FCSTD DOCUMENT  (FreeCAD 1.0R39319 (Git))
Label: 3BHK_House_Blueprint1
License: All rights reserved
LicenseURL: https://en.wikipedia.org/wiki/All_rights_reserved
objects: App::FeaturePython×51, Part::Part2DObjectPython×46
note: 46 computed .brp shape members not serialized (recipe doc carries the construction recipe); baked Part::Feature solids carry a one-line shape summary decoded from their .brp

FEATURE [Part::Part2DObjectPython] Wire  # Draft 2D object (typed FeaturePython)
  Area = 90000000
  ChamferSize = 0
  Closed = true
  End = (0,0,0)
  FilletRadius = 0
  Length = 42000
  MakeFace = true
  Points = (5) [(0,0,0),(15000,0,0),(15000,6000,0),(0,6000,0),(0,0,0)]
  Start = (0,0,0)
  Subdivisions = 0
FEATURE [Part::Part2DObjectPython] Line  # Draft 2D object (typed FeaturePython)
  Area = 0
  ChamferSize = 0
  Closed = false
  End = (3000,0,0)
  FilletRadius = 0
  Length = 1000
  MakeFace = true
  Points = (2) [(2000,0,0),(3000,0,0)]
  Start = (2000,0,0)
  Subdivisions = 0
FEATURE [Part::Part2DObjectPython] Rectangle  # Draft 2D object (typed FeaturePython)
  Area = 960000
  ChamferSize = 0
  Columns = 1
  FilletRadius = 0
  Height = 1200
  Length = 800
  MakeFace = true
  Placement = pos=(4000,1000,0) rot=(0,0,1;0rad)
  Rows = 1
FEATURE [Part::Part2DObjectPython] Rectangle001  # Draft 2D object (typed FeaturePython)
  Area = 960000
  ChamferSize = 0
  Columns = 1
  FilletRadius = 0
  Height = 1200
  Length = 800
  MakeFace = true
  Placement = pos=(9000,1000,0) rot=(0,0,1;0rad)
  Rows = 1
FEATURE [App::FeaturePython] Dimension  # Draft dimension (typed FeaturePython)
  Diameter = false
  Dimline = (7500,-500,0)
  Direction = (0,0,0)
  Distance = 15000
  End = (15000,-500,0)
  Normal = (0,0,1)
  Start = (0,-500,0)
FEATURE [App::FeaturePython] Dimension001  # Draft dimension (typed FeaturePython)
  Diameter = false
  Dimline = (0,3000,0)
  Direction = (0,0,0)
  Distance = 6000
  End = (0,6000,0)
  Normal = (0,0,1)
  Start = (0,0,0)
FEATURE [App::FeaturePython] Text  # WARN: FeaturePython — macro-defined, semantics opaque (R4)
  Placement = pos=(2500,-500,0) rot=(0,0,1;0rad)
  Text = Main Door
FEATURE [App::FeaturePython] Text001  # WARN: FeaturePython — macro-defined, semantics opaque (R4)
  Placement = pos=(4500,1500,0) rot=(0,0,1;0rad)
  Text = Window 1
FEATURE [App::FeaturePython] Text002  # WARN: FeaturePython — macro-defined, semantics opaque (R4)
  Placement = pos=(9500,1500,0) rot=(0,0,1;0rad)
  Text = Window 2
FEATURE [Part::Part2DObjectPython] Rectangle002  # Draft 2D object (typed FeaturePython)
  Area = 1.2e+07
  ChamferSize = 0
  Columns = 1
  FilletRadius = 0
  Height = 3000
  Length = 4000
  MakeFace = true
  Placement = pos=(2000,10000,0) rot=(0,0,1;0rad)
  Rows = 1
FEATURE [Part::Part2DObjectPython] Rectangle003  # Draft 2D object (typed FeaturePython)
  Area = 4e+06
  ChamferSize = 0
  Columns = 1
  FilletRadius = 0
  Height = 2000
  Length = 2000
  MakeFace = true
  Placement = pos=(8000,10000,0) rot=(0,0,1;0rad)
  Rows = 1
FEATURE [Part::Part2DObjectPython] Rectangle004  # Draft 2D object (typed FeaturePython)
  Area = 9000000
  ChamferSize = 0
  Columns = 1
  FilletRadius = 0
  Height = 3000
  Length = 3000
  MakeFace = true
  Placement = pos=(2000,13000,0) rot=(0,0,1;0rad)
  Rows = 1
FEATURE [Part::Part2DObjectPython] Rectangle005  # Draft 2D object (typed FeaturePython)
  Area = 9000000
  ChamferSize = 0
  Columns = 1
  FilletRadius = 0
  Height = 3000
  Length = 3000
  MakeFace = true
  Placement = pos=(6000,13000,0) rot=(0,0,1;0rad)
  Rows = 1
FEATURE [Part::Part2DObjectPython] Rectangle006  # Draft 2D object (typed FeaturePython)
  Area = 9000000
  ChamferSize = 0
  Columns = 1
  FilletRadius = 0
  Height = 3000
  Length = 3000
  MakeFace = true
  Placement = pos=(10000,13000,0) rot=(0,0,1;0rad)
  Rows = 1
FEATURE [Part::Part2DObjectPython] Rectangle007  # Draft 2D object (typed FeaturePython)
  Area = 2.4e+07
  ChamferSize = 0
  Columns = 1
  FilletRadius = 0
  Height = 6000
  Length = 4000
  MakeFace = true
  Placement = pos=(0,10000,0) rot=(0,0,1;0rad)
  Rows = 1
FEATURE [Part::Part2DObjectPython] Rectangle008  # Draft 2D object (typed FeaturePython)
  Area = 1.6e+07
  ChamferSize = 0
  Columns = 1
  FilletRadius = 0
  Height = 4000
  Length = 4000
  MakeFace = true
  Placement = pos=(12000,10000,0) rot=(0,0,1;0rad)
  Rows = 1
FEATURE [App::FeaturePython] Dimension002  # Draft dimension (typed FeaturePython)
  Diameter = false
  Dimline = (7500,10000,0)
  Direction = (0,0,0)
  Distance = 15000
  End = (15000,10000,0)
  Normal = (0,0,1)
  Start = (0,10000,0)
FEATURE [App::FeaturePython] Dimension003  # Draft dimension (typed FeaturePython)
  Diameter = false
  Dimline = (0,13000,0)
  Direction = (0,0,0)
  Distance = 6000
  End = (0,16000,0)
  Normal = (0,0,1)
  Start = (0,10000,0)
FEATURE [App::FeaturePython] Text003  # WARN: FeaturePython — macro-defined, semantics opaque (R4)
  Placement = pos=(3000,10500,0) rot=(0,0,1;0rad)
  Text = Living Room
FEATURE [App::FeaturePython] Text004  # WARN: FeaturePython — macro-defined, semantics opaque (R4)
  Placement = pos=(9000,10500,0) rot=(0,0,1;0rad)
  Text = Kitchen
FEATURE [App::FeaturePython] Text005  # WARN: FeaturePython — macro-defined, semantics opaque (R4)
  Placement = pos=(3000,13500,0) rot=(0,0,1;0rad)
  Text = Bedroom 1
FEATURE [App::FeaturePython] Text006  # WARN: FeaturePython — macro-defined, semantics opaque (R4)
  Placement = pos=(7000,13500,0) rot=(0,0,1;0rad)
  Text = Bedroom 2
FEATURE [App::FeaturePython] Text007  # WARN: FeaturePython — macro-defined, semantics opaque (R4)
  Placement = pos=(11000,13500,0) rot=(0,0,1;0rad)
  Text = Bedroom 3
FEATURE [App::FeaturePython] Text008  # WARN: FeaturePython — macro-defined, semantics opaque (R4)
  Placement = pos=(2000,10500,0) rot=(0,0,1;0rad)
  Text = Parking
FEATURE [App::FeaturePython] Text009  # WARN: FeaturePython — macro-defined, semantics opaque (R4)
  Placement = pos=(13000,10500,0) rot=(0,0,1;0rad)
  Text = Garden
FEATURE [Part::Part2DObjectPython] Wire001  # Draft 2D object (typed FeaturePython)
  Area = 90000000
  ChamferSize = 0
  Closed = true
  End = (0,20000,0)
  FilletRadius = 0
  Length = 42000
  MakeFace = true
  Points = (5) [(0,20000,0),(15000,20000,0),(15000,26000,0),(0,26000,0),(0,20000,0)]
  Start = (0,20000,0)
  Subdivisions = 0
FEATURE [Part::Part2DObjectPython] Line001  # Draft 2D object (typed FeaturePython)
  Area = 0
  ChamferSize = 0
  Closed = false
  End = (3000,20000,0)
  FilletRadius = 0
  Length = 1000
  MakeFace = true
  Points = (2) [(2000,20000,0),(3000,20000,0)]
  Start = (2000,20000,0)
  Subdivisions = 0
FEATURE [Part::Part2DObjectPython] Rectangle009  # Draft 2D object (typed FeaturePython)
  Area = 960000
  ChamferSize = 0
  Columns = 1
  FilletRadius = 0
  Height = 1200
  Length = 800
  MakeFace = true
  Placement = pos=(4000,21000,0) rot=(0,0,1;0rad)
  Rows = 1
FEATURE [App::FeaturePython] Dimension004  # Draft dimension (typed FeaturePython)
  Diameter = false
  Dimline = (7500,20000,0)
  Direction = (0,0,0)
  Distance = 15000
  End = (15000,20000,0)
  Normal = (0,0,1)
  Start = (0,20000,0)
FEATURE [App::FeaturePython] Dimension005  # Draft dimension (typed FeaturePython)
  Diameter = false
  Dimline = (0,23000,0)
  Direction = (0,0,0)
  Distance = 6000
  End = (0,26000,0)
  Normal = (0,0,1)
  Start = (0,20000,0)
FEATURE [App::FeaturePython] Text010  # WARN: FeaturePython — macro-defined, semantics opaque (R4)
  Placement = pos=(2500,20000,0) rot=(0,0,1;0rad)
  Text = Door 2
FEATURE [App::FeaturePython] Text011  # WARN: FeaturePython — macro-defined, semantics opaque (R4)
  Placement = pos=(4500,21000,0) rot=(0,0,1;0rad)
  Text = Window 3
FEATURE [Part::Part2DObjectPython] Line002  # Draft 2D object (typed FeaturePython)
  Area = 0
  ChamferSize = 0
  Closed = false
  End = (0,6000,0)
  FilletRadius = 0
  Length = 6000
  MakeFace = true
  Points = (2) [(0,0,0),(0,6000,0)]
  Start = (0,0,0)
  Subdivisions = 0
FEATURE [App::FeaturePython] Text012  # WARN: FeaturePython — macro-defined, semantics opaque (R4)
  Placement = pos=(0,-500,0) rot=(0,0,1;0rad)
  Text = A
FEATURE [Part::Part2DObjectPython] Line003  # Draft 2D object (typed FeaturePython)
  Area = 0
  ChamferSize = 0
  Closed = false
  End = (1000,6000,0)
  FilletRadius = 0
  Length = 6000
  MakeFace = true
  Points = (2) [(1000,0,0),(1000,6000,0)]
  Start = (1000,0,0)
  Subdivisions = 0
FEATURE [App::FeaturePython] Text013  # WARN: FeaturePython — macro-defined, semantics opaque (R4)
  Placement = pos=(1000,-500,0) rot=(0,0,1;0rad)
  Text = B
FEATURE [Part::Part2DObjectPython] Line004  # Draft 2D object (typed FeaturePython)
  Area = 0
  ChamferSize = 0
  Closed = false
  End = (2000,6000,0)
  FilletRadius = 0
  Length = 6000
  MakeFace = true
  Points = (2) [(2000,0,0),(2000,6000,0)]
  Start = (2000,0,0)
  Subdivisions = 0
FEATURE [App::FeaturePython] Text014  # WARN: FeaturePython — macro-defined, semantics opaque (R4)
  Placement = pos=(2000,-500,0) rot=(0,0,1;0rad)
  Text = C
FEATURE [Part::Part2DObjectPython] Line005  # Draft 2D object (typed FeaturePython)
  Area = 0
  ChamferSize = 0
  Closed = false
  End = (3000,6000,0)
  FilletRadius = 0
  Length = 6000
  MakeFace = true
  Points = (2) [(3000,0,0),(3000,6000,0)]
  Start = (3000,0,0)
  Subdivisions = 0
FEATURE [App::FeaturePython] Text015  # WARN: FeaturePython — macro-defined, semantics opaque (R4)
  Placement = pos=(3000,-500,0) rot=(0,0,1;0rad)
  Text = D
FEATURE [Part::Part2DObjectPython] Line006  # Draft 2D object (typed FeaturePython)
  Area = 0
  ChamferSize = 0
  Closed = false
  End = (4000,6000,0)
  FilletRadius = 0
  Length = 6000
  MakeFace = true
  Points = (2) [(4000,0,0),(4000,6000,0)]
  Start = (4000,0,0)
  Subdivisions = 0
FEATURE [App::FeaturePython] Text016  # WARN: FeaturePython — macro-defined, semantics opaque (R4)
  Placement = pos=(4000,-500,0) rot=(0,0,1;0rad)
  Text = E
FEATURE [Part::Part2DObjectPython] Line007  # Draft 2D object (typed FeaturePython)
  Area = 0
  ChamferSize = 0
  Closed = false
  End = (5000,6000,0)
  FilletRadius = 0
  Length = 6000
  MakeFace = true
  Points = (2) [(5000,0,0),(5000,6000,0)]
  Start = (5000,0,0)
  Subdivisions = 0
FEATURE [App::FeaturePython] Text017  # WARN: FeaturePython — macro-defined, semantics opaque (R4)
  Placement = pos=(5000,-500,0) rot=(0,0,1;0rad)
  Text = F
FEATURE [Part::Part2DObjectPython] Line008  # Draft 2D object (typed FeaturePython)
  Area = 0
  ChamferSize = 0
  Closed = false
  End = (6000,6000,0)
  FilletRadius = 0
  Length = 6000
  MakeFace = true
  Points = (2) [(6000,0,0),(6000,6000,0)]
  Start = (6000,0,0)
  Subdivisions = 0
FEATURE [App::FeaturePython] Text018  # WARN: FeaturePython — macro-defined, semantics opaque (R4)
  Placement = pos=(6000,-500,0) rot=(0,0,1;0rad)
  Text = G
FEATURE [Part::Part2DObjectPython] Line009  # Draft 2D object (typed FeaturePython)
  Area = 0
  ChamferSize = 0
  Closed = false
  End = (7000,6000,0)
  FilletRadius = 0
  Length = 6000
  MakeFace = true
  Points = (2) [(7000,0,0),(7000,6000,0)]
  Start = (7000,0,0)
  Subdivisions = 0
FEATURE [App::FeaturePython] Text019  # WARN: FeaturePython — macro-defined, semantics opaque (R4)
  Placement = pos=(7000,-500,0) rot=(0,0,1;0rad)
  Text = H
FEATURE [Part::Part2DObjectPython] Line010  # Draft 2D object (typed FeaturePython)
  Area = 0
  ChamferSize = 0
  Closed = false
  End = (8000,6000,0)
  FilletRadius = 0
  Length = 6000
  MakeFace = true
  Points = (2) [(8000,0,0),(8000,6000,0)]
  Start = (8000,0,0)
  Subdivisions = 0
FEATURE [App::FeaturePython] Text020  # WARN: FeaturePython — macro-defined, semantics opaque (R4)
  Placement = pos=(8000,-500,0) rot=(0,0,1;0rad)
  Text = I
FEATURE [Part::Part2DObjectPython] Line011  # Draft 2D object (typed FeaturePython)
  Area = 0
  ChamferSize = 0
  Closed = false
  End = (9000,6000,0)
  FilletRadius = 0
  Length = 6000
  MakeFace = true
  Points = (2) [(9000,0,0),(9000,6000,0)]
  Start = (9000,0,0)
  Subdivisions = 0
FEATURE [App::FeaturePython] Text021  # WARN: FeaturePython — macro-defined, semantics opaque (R4)
  Placement = pos=(9000,-500,0) rot=(0,0,1;0rad)
  Text = J
FEATURE [Part::Part2DObjectPython] Line012  # Draft 2D object (typed FeaturePython)
  Area = 0
  ChamferSize = 0
  Closed = false
  End = (10000,6000,0)
  FilletRadius = 0
  Length = 6000
  MakeFace = true
  Points = (2) [(10000,0,0),(10000,6000,0)]
  Start = (10000,0,0)
  Subdivisions = 0
FEATURE [App::FeaturePython] Text022  # WARN: FeaturePython — macro-defined, semantics opaque (R4)
  Placement = pos=(10000,-500,0) rot=(0,0,1;0rad)
  Text = K
FEATURE [Part::Part2DObjectPython] Line013  # Draft 2D object (typed FeaturePython)
  Area = 0
  ChamferSize = 0
  Closed = false
  End = (11000,6000,0)
  FilletRadius = 0
  Length = 6000
  MakeFace = true
  Points = (2) [(11000,0,0),(11000,6000,0)]
  Start = (11000,0,0)
  Subdivisions = 0
FEATURE [App::FeaturePython] Text023  # WARN: FeaturePython — macro-defined, semantics opaque (R4)
  Placement = pos=(11000,-500,0) rot=(0,0,1;0rad)
  Text = L
FEATURE [Part::Part2DObjectPython] Line014  # Draft 2D object (typed FeaturePython)
  Area = 0
  ChamferSize = 0
  Closed = false
  End = (12000,6000,0)
  FilletRadius = 0
  Length = 6000
  MakeFace = true
  Points = (2) [(12000,0,0),(12000,6000,0)]
  Start = (12000,0,0)
  Subdivisions = 0
FEATURE [App::FeaturePython] Text024  # WARN: FeaturePython — macro-defined, semantics opaque (R4)
  Placement = pos=(12000,-500,0) rot=(0,0,1;0rad)
  Text = M
FEATURE [Part::Part2DObjectPython] Line015  # Draft 2D object (typed FeaturePython)
  Area = 0
  ChamferSize = 0
  Closed = false
  End = (13000,6000,0)
  FilletRadius = 0
  Length = 6000
  MakeFace = true
  Points = (2) [(13000,0,0),(13000,6000,0)]
  Start = (13000,0,0)
  Subdivisions = 0
FEATURE [App::FeaturePython] Text025  # WARN: FeaturePython — macro-defined, semantics opaque (R4)
  Placement = pos=(13000,-500,0) rot=(0,0,1;0rad)
  Text = N
FEATURE [Part::Part2DObjectPython] Line016  # Draft 2D object (typed FeaturePython)
  Area = 0
  ChamferSize = 0
  Closed = false
  End = (14000,6000,0)
  FilletRadius = 0
  Length = 6000
  MakeFace = true
  Points = (2) [(14000,0,0),(14000,6000,0)]
  Start = (14000,0,0)
  Subdivisions = 0
FEATURE [App::FeaturePython] Text026  # WARN: FeaturePython — macro-defined, semantics opaque (R4)
  Placement = pos=(14000,-500,0) rot=(0,0,1;0rad)
  Text = O
FEATURE [Part::Part2DObjectPython] Line017  # Draft 2D object (typed FeaturePython)
  Area = 0
  ChamferSize = 0
  Closed = false
  End = (15000,6000,0)
  FilletRadius = 0
  Length = 6000
  MakeFace = true
  Points = (2) [(15000,0,0),(15000,6000,0)]
  Start = (15000,0,0)
  Subdivisions = 0
FEATURE [App::FeaturePython] Text027  # WARN: FeaturePython — macro-defined, semantics opaque (R4)
  Placement = pos=(15000,-500,0) rot=(0,0,1;0rad)
  Text = P
FEATURE [Part::Part2DObjectPython] Line018  # Draft 2D object (typed FeaturePython)
  Area = 0
  ChamferSize = 0
  Closed = false
  End = (15000,0,0)
  FilletRadius = 0
  Length = 15000
  MakeFace = true
  Points = (2) [(0,0,0),(15000,0,0)]
  Start = (0,0,0)
  Subdivisions = 0
FEATURE [App::FeaturePython] Text028  # WARN: FeaturePython — macro-defined, semantics opaque (R4)
  Placement = pos=(-500,0,0) rot=(0,0,1;0rad)
  Text = 1
FEATURE [Part::Part2DObjectPython] Line019  # Draft 2D object (typed FeaturePython)
  Area = 0
  ChamferSize = 0
  Closed = false
  End = (15000,1000,0)
  FilletRadius = 0
  Length = 15000
  MakeFace = true
  Points = (2) [(0,1000,0),(15000,1000,0)]
  Start = (0,1000,0)
  Subdivisions = 0
FEATURE [App::FeaturePython] Text029  # WARN: FeaturePython — macro-defined, semantics opaque (R4)
  Placement = pos=(-500,1000,0) rot=(0,0,1;0rad)
  Text = 2
FEATURE [Part::Part2DObjectPython] Line020  # Draft 2D object (typed FeaturePython)
  Area = 0
  ChamferSize = 0
  Closed = false
  End = (15000,2000,0)
  FilletRadius = 0
  Length = 15000
  MakeFace = true
  Points = (2) [(0,2000,0),(15000,2000,0)]
  Start = (0,2000,0)
  Subdivisions = 0
FEATURE [App::FeaturePython] Text030  # WARN: FeaturePython — macro-defined, semantics opaque (R4)
  Placement = pos=(-500,2000,0) rot=(0,0,1;0rad)
  Text = 3
FEATURE [Part::Part2DObjectPython] Line021  # Draft 2D object (typed FeaturePython)
  Area = 0
  ChamferSize = 0
  Closed = false
  End = (15000,3000,0)
  FilletRadius = 0
  Length = 15000
  MakeFace = true
  Points = (2) [(0,3000,0),(15000,3000,0)]
  Start = (0,3000,0)
  Subdivisions = 0
FEATURE [App::FeaturePython] Text031  # WARN: FeaturePython — macro-defined, semantics opaque (R4)
  Placement = pos=(-500,3000,0) rot=(0,0,1;0rad)
  Text = 4
FEATURE [Part::Part2DObjectPython] Line022  # Draft 2D object (typed FeaturePython)
  Area = 0
  ChamferSize = 0
  Closed = false
  End = (15000,4000,0)
  FilletRadius = 0
  Length = 15000
  MakeFace = true
  Points = (2) [(0,4000,0),(15000,4000,0)]
  Start = (0,4000,0)
  Subdivisions = 0
FEATURE [App::FeaturePython] Text032  # WARN: FeaturePython — macro-defined, semantics opaque (R4)
  Placement = pos=(-500,4000,0) rot=(0,0,1;0rad)
  Text = 5
FEATURE [Part::Part2DObjectPython] Line023  # Draft 2D object (typed FeaturePython)
  Area = 0
  ChamferSize = 0
  Closed = false
  End = (15000,5000,0)
  FilletRadius = 0
  Length = 15000
  MakeFace = true
  Points = (2) [(0,5000,0),(15000,5000,0)]
  Start = (0,5000,0)
  Subdivisions = 0
FEATURE [App::FeaturePython] Text033  # WARN: FeaturePython — macro-defined, semantics opaque (R4)
  Placement = pos=(-500,5000,0) rot=(0,0,1;0rad)
  Text = 6
FEATURE [Part::Part2DObjectPython] Line024  # Draft 2D object (typed FeaturePython)
  Area = 0
  ChamferSize = 0
  Closed = false
  End = (15000,6000,0)
  FilletRadius = 0
  Length = 15000
  MakeFace = true
  Points = (2) [(0,6000,0),(15000,6000,0)]
  Start = (0,6000,0)
  Subdivisions = 0
FEATURE [App::FeaturePython] Text034  # WARN: FeaturePython — macro-defined, semantics opaque (R4)
  Placement = pos=(-500,6000,0) rot=(0,0,1;0rad)
  Text = 7
FEATURE [Part::Part2DObjectPython] Line025  # Draft 2D object (typed FeaturePython)
  Area = 0
  ChamferSize = 0
  Closed = false
  End = (15000,7000,0)
  FilletRadius = 0
  Length = 15000
  MakeFace = true
  Points = (2) [(0,7000,0),(15000,7000,0)]
  Start = (0,7000,0)
  Subdivisions = 0
FEATURE [App::FeaturePython] Text035  # WARN: FeaturePython — macro-defined, semantics opaque (R4)
  Placement = pos=(-500,7000,0) rot=(0,0,1;0rad)
  Text = 8
FEATURE [Part::Part2DObjectPython] Line026  # Draft 2D object (typed FeaturePython)
  Area = 0
  ChamferSize = 0
  Closed = false
  End = (15000,8000,0)
  FilletRadius = 0
  Length = 15000
  MakeFace = true
  Points = (2) [(0,8000,0),(15000,8000,0)]
  Start = (0,8000,0)
  Subdivisions = 0
FEATURE [App::FeaturePython] Text036  # WARN: FeaturePython — macro-defined, semantics opaque (R4)
  Placement = pos=(-500,8000,0) rot=(0,0,1;0rad)
  Text = 9
FEATURE [Part::Part2DObjectPython] Line027  # Draft 2D object (typed FeaturePython)
  Area = 0
  ChamferSize = 0
  Closed = false
  End = (15000,9000,0)
  FilletRadius = 0
  Length = 15000
  MakeFace = true
  Points = (2) [(0,9000,0),(15000,9000,0)]
  Start = (0,9000,0)
  Subdivisions = 0
FEATURE [App::FeaturePython] Text037  # WARN: FeaturePython — macro-defined, semantics opaque (R4)
  Placement = pos=(-500,9000,0) rot=(0,0,1;0rad)
  Text = 10
FEATURE [Part::Part2DObjectPython] Line028  # Draft 2D object (typed FeaturePython)
  Area = 0
  ChamferSize = 0
  Closed = false
  End = (15000,10000,0)
  FilletRadius = 0
  Length = 15000
  MakeFace = true
  Points = (2) [(0,10000,0),(15000,10000,0)]
  Start = (0,10000,0)
  Subdivisions = 0
FEATURE [App::FeaturePython] Text038  # WARN: FeaturePython — macro-defined, semantics opaque (R4)
  Placement = pos=(-500,10000,0) rot=(0,0,1;0rad)
  Text = 11
FEATURE [Part::Part2DObjectPython] Line029  # Draft 2D object (typed FeaturePython)
  Area = 0
  ChamferSize = 0
  Closed = false
  End = (15000,11000,0)
  FilletRadius = 0
  Length = 15000
  MakeFace = true
  Points = (2) [(0,11000,0),(15000,11000,0)]
  Start = (0,11000,0)
  Subdivisions = 0
FEATURE [App::FeaturePython] Text039  # WARN: FeaturePython — macro-defined, semantics opaque (R4)
  Placement = pos=(-500,11000,0) rot=(0,0,1;0rad)
  Text = 12
FEATURE [Part::Part2DObjectPython] Line030  # Draft 2D object (typed FeaturePython)
  Area = 0
  ChamferSize = 0
  Closed = false
  End = (15000,12000,0)
  FilletRadius = 0
  Length = 15000
  MakeFace = true
  Points = (2) [(0,12000,0),(15000,12000,0)]
  Start = (0,12000,0)
  Subdivisions = 0
FEATURE [App::FeaturePython] Text040  # WARN: FeaturePython — macro-defined, semantics opaque (R4)
  Placement = pos=(-500,12000,0) rot=(0,0,1;0rad)
  Text = 13
FEATURE [Part::Part2DObjectPython] Line031  # Draft 2D object (typed FeaturePython)
  Area = 0
  ChamferSize = 0
  Closed = false
  End = (15000,13000,0)
  FilletRadius = 0
  Length = 15000
  MakeFace = true
  Points = (2) [(0,13000,0),(15000,13000,0)]
  Start = (0,13000,0)
  Subdivisions = 0
FEATURE [App::FeaturePython] Text041  # WARN: FeaturePython — macro-defined, semantics opaque (R4)
  Placement = pos=(-500,13000,0) rot=(0,0,1;0rad)
  Text = 14
FEATURE [Part::Part2DObjectPython] Line032  # Draft 2D object (typed FeaturePython)
  Area = 0
  ChamferSize = 0
  Closed = false
  End = (15000,14000,0)
  FilletRadius = 0
  Length = 15000
  MakeFace = true
  Points = (2) [(0,14000,0),(15000,14000,0)]
  Start = (0,14000,0)
  Subdivisions = 0
FEATURE [App::FeaturePython] Text042  # WARN: FeaturePython — macro-defined, semantics opaque (R4)
  Placement = pos=(-500,14000,0) rot=(0,0,1;0rad)
  Text = 15
FEATURE [Part::Part2DObjectPython] Line033  # Draft 2D object (typed FeaturePython)
  Area = 0
  ChamferSize = 0
  Closed = false
  End = (15000,15000,0)
  FilletRadius = 0
  Length = 15000
  MakeFace = true
  Points = (2) [(0,15000,0),(15000,15000,0)]
  Start = (0,15000,0)
  Subdivisions = 0
FEATURE [App::FeaturePython] Text043  # WARN: FeaturePython — macro-defined, semantics opaque (R4)
  Placement = pos=(-500,15000,0) rot=(0,0,1;0rad)
  Text = 16
FEATURE [App::FeaturePython] Text044  # WARN: FeaturePython — macro-defined, semantics opaque (R4)
  Placement = pos=(12000,-1000,0) rot=(0,0,1;0rad)
  Text = 3BHK House Blueprint | Scale: 1:100 | Date: 2024-09-16
